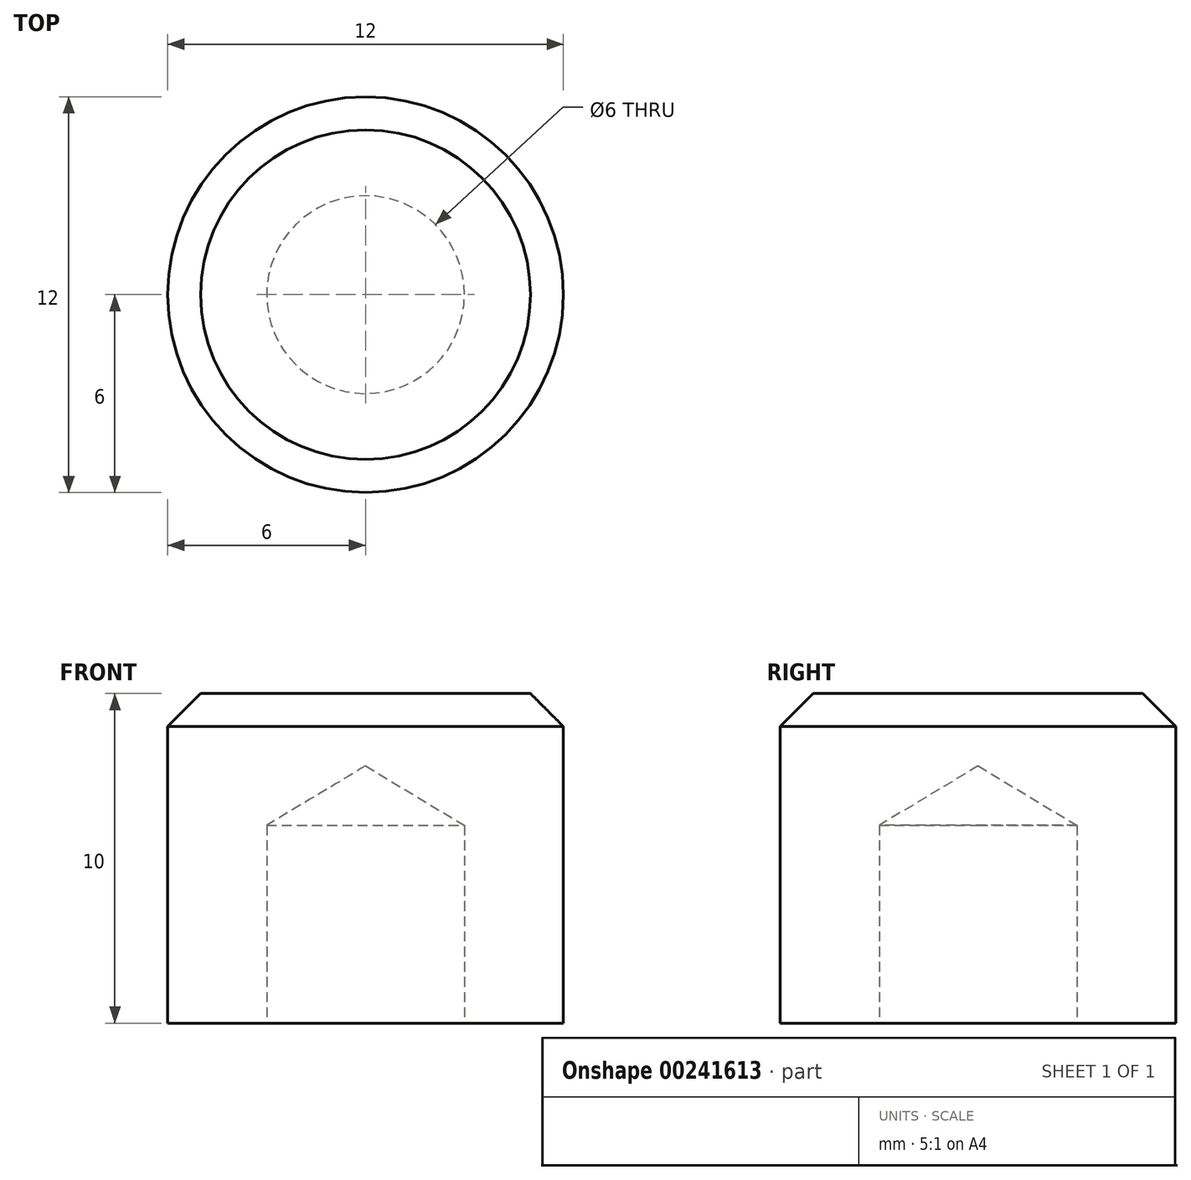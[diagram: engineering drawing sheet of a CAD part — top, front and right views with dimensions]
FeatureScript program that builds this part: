
annotation { "Feature Type Name" : "Feature", "Feature Type Description" : "" }
export const myFeature = defineFeature(function(context is Context, id is Id, definition is map)
    precondition{}
    {
        {
            var Q0;
            Q0=qCreatedBy(makeId("Top.planeOp"),FACE);
            var sketch = newSketch(context, id + "F0", { "sketchPlane" : qUnion([Q0])});
            skCircle(sketch, "E0", {"center": v(0, 0) * mm, "radius": 6 * mm});
            skSolve(sketch);
        }
        {
            var Q0;
            Q0 = qSketchRegion(id + "F0", true);
            extrude(context, id + "F1", {"entities" : qUnion([Q0]), "depth" : 10 * mm});
        }
        {
            var Q0;
            Q0=makeQuery(id+"F1.opExtrude","CAP_EDGE",EDGE,{"disambiguationData":[OSD([sQuery(id+"F0.wireOp",EDGE,"E0")])],"isStart":false});
            chamfer(context, id + "F2", {"entities" : qUnion([Q0]), "width" : 1 * mm, "tangentPropagation" : true});
        }
        {
            var Q0;
            Q0=makeQuery(id+"F1.opExtrude","CAP_FACE",FACE,{"disambiguationData":[OSD([sQuery(id+"F0.wireOp",EDGE,"E0")])],"isStart":true});
            var sketch = newSketch(context, id + "F3", { "sketchPlane" : qUnion([Q0])});
            skPoint(sketch, "E1", {"position": v(0, 0) * mm});
            skSolve(sketch);
        }
        {
            var Q0;
            Q0=sQuery(id+"F3.wireOp",VERTEX,"E1");
            var Q1;
            Q1=makeQuery(id+"F1.opExtrude","SWEPT_BODY",BODY,{"disambiguationData":[OSD([sQuery(id+"F0.wireOp",EDGE,"E0")])]});
            hole(context, id + "F4", {"style" : HoleStyle.SIMPLE, "endStyle" : HoleEndStyle.BLIND, "holeDiameter" : 6 * mm, "holeDepth" : 6 * mm, "startFromSketch" : true, "locations" : qUnion([Q0]), "scope" : qUnion([Q1])});
        }
    });
